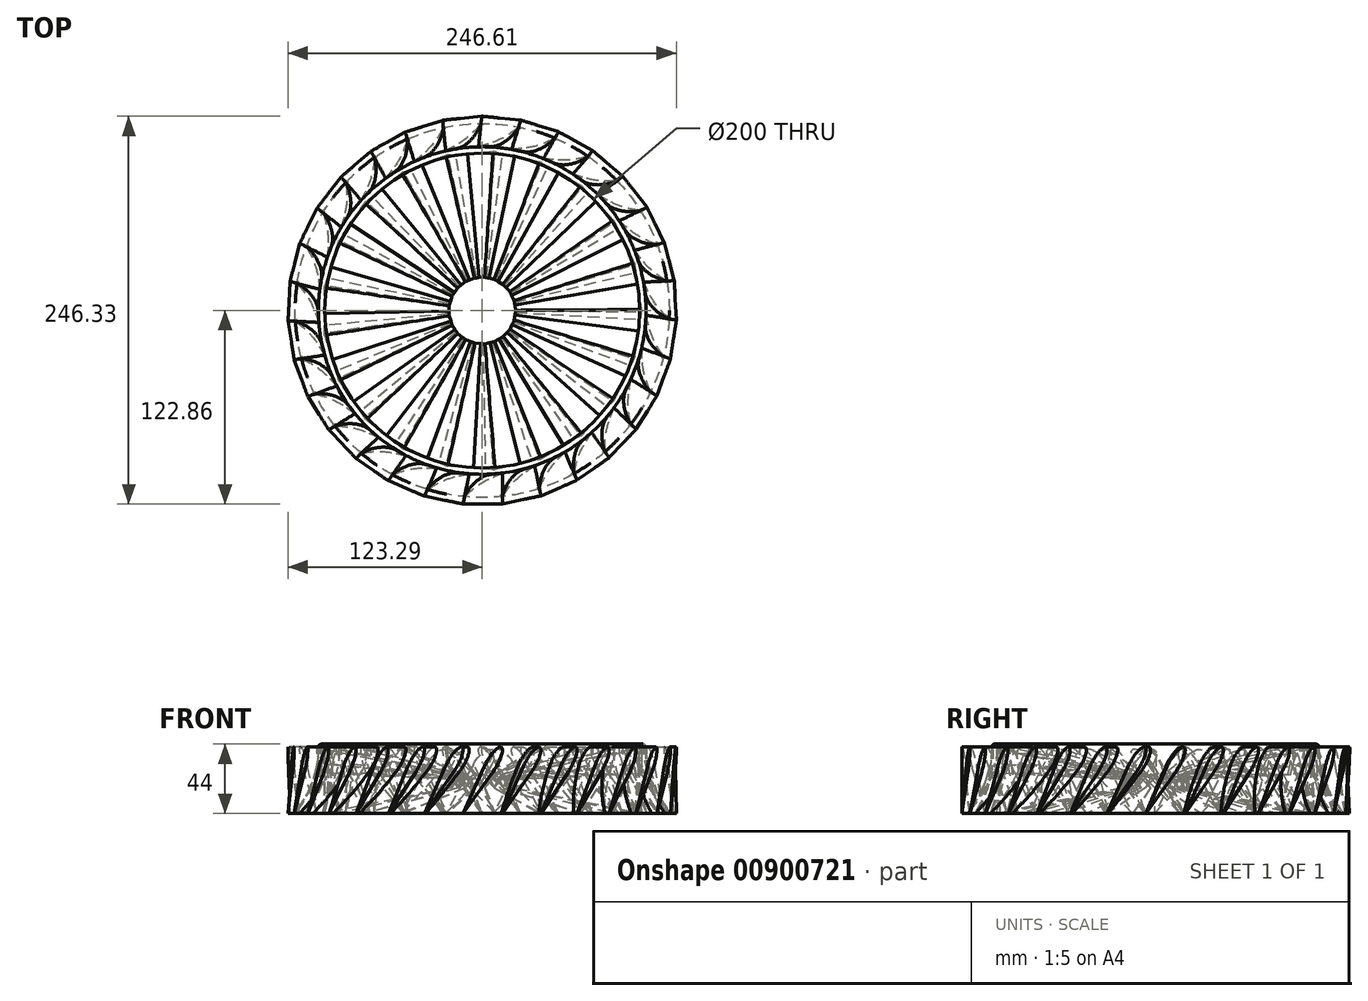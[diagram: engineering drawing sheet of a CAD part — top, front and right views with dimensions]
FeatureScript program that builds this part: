
annotation { "Feature Type Name" : "Feature", "Feature Type Description" : "" }
export const myFeature = defineFeature(function(context is Context, id is Id, definition is map)
    precondition{}
    {
        {
            var Q0;
            Q0=qCreatedBy(makeId("Right.planeOp"),FACE);
            cPlane(context, id + "F0", {"entities" : qUnion([Q0]), "cplaneType" : CPlaneType.OFFSET, "offset" : 100 * mm, "oppositeDirection" : true, "width" : 150 * mm, "height" : 150 * mm});
        }
        {
            var Q0;
            Q0=qCreatedBy(id+"F0.planeOp",FACE);
            var sketch = newSketch(context, id + "F1", { "sketchPlane" : qUnion([Q0])});
            skLineSegment(sketch, "E0.bottom", {"start": v(15.7, 0) * mm, "end": v(-15.7, 0) * mm, "construction": true});
            skLineSegment(sketch, "E0.top", {"start": v(15.7, 50) * mm, "end": v(-15.7, 50) * mm, "construction": true});
            skLineSegment(sketch, "E0.left", {"start": v(15.7, 0) * mm, "end": v(15.7, 50) * mm, "construction": true});
            skLineSegment(sketch, "E0.right", {"start": v(-15.7, 0) * mm, "end": v(-15.7, 50) * mm, "construction": true});
            skPoint(sketch, "E1", {"position": v(0, 0) * mm});
            skPoint(sketch, "E2", {"position": v(-7.7, 31.07) * mm});
            skEllipse(sketch, "E3", {"center": v(-7.7, 31.07) * mm, "majorRadius": 11.52 * mm, "minorRadius": 5 * mm, "majorAxis": v(-0.6, 0.8)});
            skLineSegment(sketch, "E4", {"start": v(-1.84, 31.22) * mm, "end": v(15.7, 0) * mm});
            skLineSegment(sketch, "E5", {"start": v(15.7, 0) * mm, "end": v(-9.47, 25.48) * mm});
            skPoint(sketch, "E6", {"position": v(-3.71, 34.08) * mm});
            skPoint(sketch, "E7", {"position": v(-11.7, 28.06) * mm});
            skLineSegment(sketch, "E8", {"start": v(-3.71, 34.08) * mm, "end": v(-7.7, 31.07) * mm, "construction": true});
            skLineSegment(sketch, "E9", {"start": v(-11.7, 28.06) * mm, "end": v(-7.7, 31.07) * mm, "construction": true});
            skLineSegment(sketch, "E10", {"start": v(-1.84, 31.22) * mm, "end": v(-9.47, 25.48) * mm, "construction": true});
            skLineSegment(sketch, "E11", {"start": v(-7.7, 31.07) * mm, "end": v(15.7, 0) * mm, "construction": true});
            skLineSegment(sketch, "E12.bottom", {"start": v(51.34, 60) * mm, "end": v(-48.66, 60) * mm});
            skLineSegment(sketch, "E12.top", {"start": v(51.34, 0) * mm, "end": v(-48.66, 0) * mm});
            skLineSegment(sketch, "E12.right", {"start": v(-48.66, 60) * mm, "end": v(-48.66, 0) * mm});
            skPoint(sketch, "E13", {"position": v(-13.05, 40.75) * mm});
            skLineSegment(sketch, "E14", {"start": v(-13.05, 40.75) * mm, "end": v(-23.99, 40.75) * mm, "construction": true});
            skLineSegment(sketch, "E15", {"start": v(-48.66, 40.75) * mm, "end": v(-48.66, 0) * mm, "construction": true});
            skPoint(sketch, "E16", {"position": v(0, 20.38) * mm});
            skPoint(sketch, "E16.positionSnap0", {"position": v(-48.66, 20.38) * mm});
            skSolve(sketch);
        }
        {
            var Q0;
            Q0=qCreatedBy(makeId("Right.planeOp"),FACE);
            cPlane(context, id + "F2", {"entities" : qUnion([Q0]), "cplaneType" : CPlaneType.OFFSET, "offset" : 21 * mm, "oppositeDirection" : true, "width" : 150 * mm, "height" : 150 * mm});
        }
        {
            var Q0;
            Q0=qCreatedBy(id+"F2.planeOp",FACE);
            var sketch = newSketch(context, id + "F3", { "sketchPlane" : qUnion([Q0])});
            skLineSegment(sketch, "E17.bottom", {"start": v(3.34, 16.04) * mm, "end": v(-3.34, 16.04) * mm, "construction": true});
            skLineSegment(sketch, "E17.top", {"start": v(3.34, 66.04) * mm, "end": v(-3.34, 66.04) * mm, "construction": true});
            skLineSegment(sketch, "E17.left", {"start": v(3.34, 16.04) * mm, "end": v(3.34, 66.04) * mm, "construction": true});
            skLineSegment(sketch, "E17.right", {"start": v(-3.34, 16.04) * mm, "end": v(-3.34, 66.04) * mm, "construction": true});
            skPoint(sketch, "E18", {"position": v(0, 16.04) * mm});
            skPoint(sketch, "E19", {"position": v(-1.64, 22.65) * mm});
            skEllipse(sketch, "E20", {"center": v(-1.64, 22.65) * mm, "majorRadius": 2.45 * mm, "minorRadius": 1.06 * mm, "majorAxis": v(-0.6, 0.8)});
            skLineSegment(sketch, "E21", {"start": v(-0.4, 22.68) * mm, "end": v(3.34, 16.04) * mm});
            skLineSegment(sketch, "E22", {"start": v(3.34, 16.04) * mm, "end": v(-2.01, 21.46) * mm});
            skPoint(sketch, "E23", {"position": v(-0.79, 23.3) * mm});
            skPoint(sketch, "E24", {"position": v(-2.49, 22.01) * mm});
            skLineSegment(sketch, "E25", {"start": v(-0.79, 23.3) * mm, "end": v(-1.64, 22.65) * mm, "construction": true});
            skLineSegment(sketch, "E26", {"start": v(-2.49, 22.01) * mm, "end": v(-1.64, 22.65) * mm, "construction": true});
            skLineSegment(sketch, "E27", {"start": v(-0.4, 22.68) * mm, "end": v(-2.01, 21.46) * mm, "construction": true});
            skLineSegment(sketch, "E28", {"start": v(-1.64, 22.65) * mm, "end": v(3.34, 16.04) * mm, "construction": true});
            skLineSegment(sketch, "E29.right", {"start": v(-42.27, -20.65) * mm, "end": v(-42.27, -80.65) * mm});
            skPoint(sketch, "E30", {"position": v(-2.78, 24.7) * mm});
            skLineSegment(sketch, "E31", {"start": v(-2.78, 24.7) * mm, "end": v(-17.6, 24.7) * mm, "construction": true});
            skLineSegment(sketch, "E32", {"start": v(-42.27, 24.7) * mm, "end": v(-42.27, -80.65) * mm, "construction": true});
            skPoint(sketch, "E33", {"position": v(6.4, -27.97) * mm});
            skPoint(sketch, "E33.positionSnap0", {"position": v(-42.27, -27.97) * mm});
            skLineSegment(sketch, "E34", {"start": v(-14.15, 16.04) * mm, "end": v(-14.15, 24.7) * mm, "construction": true});
            skPoint(sketch, "E35", {"position": v(0, 20.38) * mm});
            skPoint(sketch, "E35.positionSnap0", {"position": v(-14.15, 20.38) * mm});
            skSolve(sketch);
        }
        {
            var Q0;
            Q0 = qSketchRegion(id + "F3", true);
            var Q1;
            Q1 = qSketchRegion(id + "F1", true);
            loft(context, id + "F4", {"sheetProfilesArray" : [{ "sheetProfileEntities" : qUnion([Q0]) }, { "sheetProfileEntities" : qUnion([Q1]) }]});
        }
        {
            var Q0;
            Q0=qCreatedBy(makeId("Right.planeOp"),FACE);
            var sketch = newSketch(context, id + "F5", { "sketchPlane" : qUnion([Q0])});
            skLineSegment(sketch, "E36", {"start": v(0, 0) * mm, "end": v(0, 11.65) * mm, "construction": true});
            skPoint(sketch, "E37", {"position": v(-100, 0) * mm});
            skPoint(sketch, "E38", {"position": v(-100, 42) * mm});
            skLineSegment(sketch, "E39", {"start": v(-100, 42) * mm, "end": v(-100, 31.5) * mm});
            skPoint(sketch, "E40", {"position": v(-102, 42) * mm});
            skArc(sketch, "E41", {"start": v(-100, 42) * mm, "mid": v(-102, 44) * mm, "end": v(-104, 42) * mm});
            skArc(sketch, "E42", {"start": v(-118.59, 1.64) * mm, "mid": v(-107.76, 20.54) * mm, "end": v(-104, 42) * mm});
            skLineSegment(sketch, "E43", {"start": v(-117.82, 0) * mm, "end": v(-115.46, 0) * mm});
            skPoint(sketch, "E44.visualSharp", {"position": v(-120, 0) * mm});
            skArc(sketch, "E44.filletArc", {"start": v(-118.59, 1.64) * mm, "mid": v(-118.73, 0.58) * mm, "end": v(-117.82, 0) * mm});
            skArc(sketch, "E45", {"start": v(-111.8, 1.59) * mm, "mid": v(-103.06, 15.42) * mm, "end": v(-100, 31.5) * mm});
            skPoint(sketch, "E46.orphan", {"position": v(-100, 21) * mm});
            skPoint(sketch, "E47.orphan", {"position": v(-108.9, 0) * mm});
            skPoint(sketch, "E48.visualSharp", {"position": v(-113.36, 0) * mm});
            skArc(sketch, "E48.filletArc", {"start": v(-115.46, 0) * mm, "mid": v(-113.47, 0.41) * mm, "end": v(-111.8, 1.59) * mm});
            skPoint(sketch, "E49", {"position": v(-118.82, 1.08) * mm});
            skSolve(sketch);
        }
        {
            var Q0;
            {var subQ0=sQuery(id+"F3.wireOp",EDGE,"E20");var subQ1=makeQuery(id+"F3.imprint","INTERSECT",VERTEX,{"derivedFrom":[subQ0,sQuery(id+"F3.wireOp",EDGE,"E21")]});var subQ3=sQuery(id+"F1.wireOp",EDGE,"E3");var subQ4=makeQuery(id+"F1.imprint","INTERSECT",VERTEX,{"derivedFrom":[subQ3,sQuery(id+"F1.wireOp",EDGE,"E4")]});Q0=makeQuery(id+"F4.opLoft","SWEPT_BODY",BODY,{"disambiguationData":[OSD([makeQuery(id+"F1.imprint","IMPRINT",FACE,{"disambiguationData":[TD([[makeQuery(id+"F1.imprint","IMPRINT",EDGE,{"disambiguationData":[TD([[subQ4,1.0]])],"derivedFrom":subQ3}),1.0]])]}),makeQuery(id+"F3.imprint","IMPRINT",FACE,{"disambiguationData":[TD([[makeQuery(id+"F3.imprint","IMPRINT",EDGE,{"disambiguationData":[TD([[subQ1,1.0]])],"derivedFrom":subQ0}),1.0]])]})])]});}
            var Q1;
            Q1=sQuery(id+"F5.wireOp",EDGE,"E36");
            circularPattern(context, id + "F6", {"entities" : qUnion([Q0]), "axis" : qUnion([Q1]), "angle" : 360 * degree, "instanceCount" : 21, "equalSpace" : true});
        }
        {
            var Q0;
            Q0=makeQuery(id+"F5.imprint","IMPRINT",FACE,{"disambiguationData":[TD([[makeQuery(id+"F5.imprint","IMPRINT",EDGE,{"derivedFrom":sQuery(id+"F5.wireOp",EDGE,"E39")}),-1.0]])]});
            var Q1;
            Q1=sQuery(id+"F5.wireOp",EDGE,"E36");
            revolve(context, id + "F7", {"surfaceOperationType" : NewSurfaceOperationType.NEW, "entities" : qUnion([Q0]), "axis" : qUnion([Q1]), "revolveType" : RevolveType.FULL, "oppositeDirection" : true});
        }
        {
            var Q0;
            Q0=qCreatedBy(makeId("Front.planeOp"),FACE);
            cPlane(context, id + "F8", {"entities" : qUnion([Q0]), "cplaneType" : CPlaneType.OFFSET, "offset" : 122.8 * mm, "width" : 150 * mm, "height" : 150 * mm});
        }
        {
            var Q0;
            Q0=qCreatedBy(id+"F8.planeOp",FACE);
            var sketch = newSketch(context, id + "F9", { "sketchPlane" : qUnion([Q0])});
            skPoint(sketch, "E50", {"position": v(0, 42) * mm});
            skPoint(sketch, "E51", {"position": v(12.12, 42) * mm});
            skPoint(sketch, "E52", {"position": v(-12.12, 0) * mm});
            skLineSegment(sketch, "E53", {"start": v(12.12, 42) * mm, "end": v(-12.12, 0) * mm, "construction": true});
            skLineSegment(sketch, "E54", {"start": v(0, 0) * mm, "end": v(35.61, 0) * mm, "construction": true});
            skPoint(sketch, "E55", {"position": v(0, 21) * mm});
            skLineSegment(sketch, "E56", {"start": v(0, 21) * mm, "end": v(12.12, 42) * mm, "construction": true});
            skPoint(sketch, "E57", {"position": v(6.06, 31.5) * mm});
            skEllipse(sketch, "E58", {"center": v(6.06, 31.5) * mm, "majorRadius": 12.12 * mm, "minorRadius": 3.4 * mm, "majorAxis": v(0.5, 0.87)});
            skLineSegment(sketch, "E59", {"start": v(-12.12, 0) * mm, "end": v(1.27, 29.6) * mm});
            skLineSegment(sketch, "E60", {"start": v(-12.12, 0) * mm, "end": v(6.82, 26.4) * mm});
            skPoint(sketch, "E61", {"position": v(3.12, 33.2) * mm});
            skPoint(sketch, "E62", {"position": v(9, 29.8) * mm});
            skLineSegment(sketch, "E63", {"start": v(3.12, 33.2) * mm, "end": v(9, 29.8) * mm, "construction": true});
            skLineSegment(sketch, "E64", {"start": v(1.27, 29.6) * mm, "end": v(6.82, 26.4) * mm, "construction": true});
            skSolve(sketch);
        }
        {
            var Q0;
            Q0 = qSketchRegion(id + "F9", true);
            var Q1;
            Q1=makeQuery(id+"F7.opRevolve","SWEPT_FACE",FACE,{"disambiguationData":[OSD([sQuery(id+"F5.wireOp",EDGE,"E42")])]});
            var Q2;
            Q2=makeQuery(id+"F7.opRevolve","SWEPT_BODY",BODY,{"disambiguationData":[OSD([sQuery(id+"F5.wireOp",EDGE,"E39"),sQuery(id+"F5.wireOp",EDGE,"E41"),sQuery(id+"F5.wireOp",EDGE,"E42"),sQuery(id+"F5.wireOp",EDGE,"E43"),sQuery(id+"F5.wireOp",EDGE,"E44.filletArc"),sQuery(id+"F5.wireOp",EDGE,"E45"),sQuery(id+"F5.wireOp",EDGE,"E48.filletArc")])]});
            extrude(context, id + "F10", {"entities" : qUnion([Q0]), "endBound" : BoundingType.UP_TO_BODY, "oppositeDirection" : true, "depth" : 25 * mm, "endBoundEntityFace" : qUnion([Q1]), "endBoundEntityBody" : qUnion([Q2]), "offsetDistance" : 25 * mm});
        }
        {
            var Q0;
            Q0=makeQuery(id+"F10.opExtrude","SWEPT_BODY",BODY,{"disambiguationData":[OSD([sQuery(id+"F9.wireOp",EDGE,"E58"),sQuery(id+"F9.wireOp",EDGE,"E59"),sQuery(id+"F9.wireOp",EDGE,"E60")])]});
            var Q1;
            Q1=sQuery(id+"F5.wireOp",EDGE,"E36");
            circularPattern(context, id + "F11", {"entities" : qUnion([Q0]), "axis" : qUnion([Q1]), "angle" : 360 * degree, "instanceCount" : 31, "equalSpace" : true});
        }
    });
